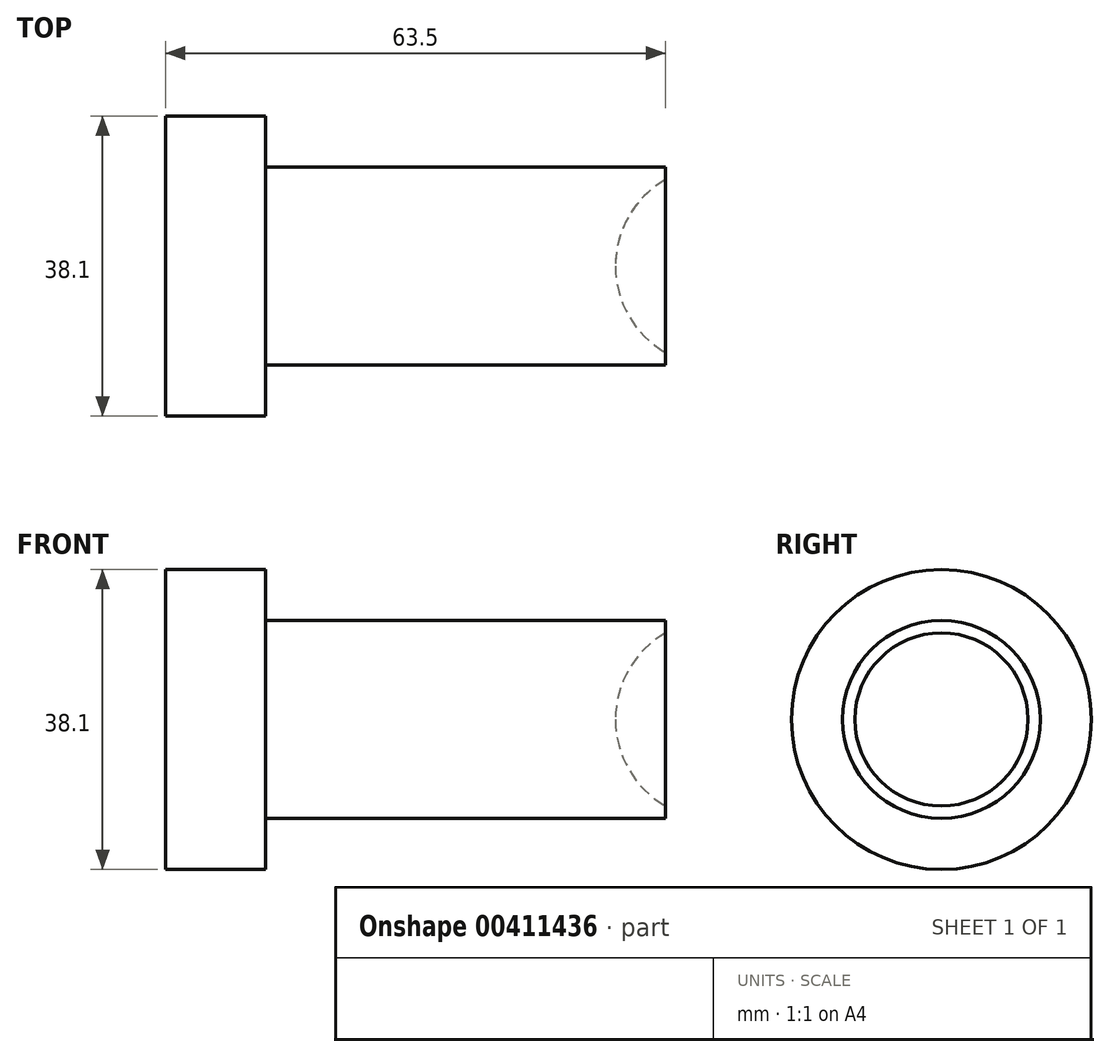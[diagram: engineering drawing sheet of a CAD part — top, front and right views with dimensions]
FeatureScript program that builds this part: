
annotation { "Feature Type Name" : "Feature", "Feature Type Description" : "" }
export const myFeature = defineFeature(function(context is Context, id is Id, definition is map)
    precondition{}
    {
        {
            var Q0;
            Q0=qCreatedBy(makeId("Right.planeOp"),FACE);
            var sketch = newSketch(context, id + "F0", { "sketchPlane" : qUnion([Q0])});
            skCircle(sketch, "E0", {"center": v(0, 0) * mm, "radius": 19.05 * mm});
            skSolve(sketch);
        }
        {
            var Q0;
            Q0 = qSketchRegion(id + "F0", true);
            extrude(context, id + "F1", {"entities" : qUnion([Q0]), "depth" : 12.7 * mm});
        }
        {
            var Q0;
            Q0=makeQuery(id+"F1.opExtrude","CAP_FACE",FACE,{"disambiguationData":[OSD([sQuery(id+"F0.wireOp",EDGE,"E0")])],"isStart":false});
            var sketch = newSketch(context, id + "F2", { "sketchPlane" : qUnion([Q0])});
            skCircle(sketch, "E1", {"center": v(0, 0) * mm, "radius": 12.57 * mm});
            skSolve(sketch);
        }
        {
            var Q0;
            Q0 = qSketchRegion(id + "F2", true);
            extrude(context, id + "F3", {"entities" : qUnion([Q0]), "operationType" : NewBodyOperationType.ADD, "depth" : 50.8 * mm});
        }
        {
            var Q0;
            Q0=qCreatedBy(makeId("Top.planeOp"),FACE);
            var sketch = newSketch(context, id + "F4", { "sketchPlane" : qUnion([Q0])});
            skArc(sketch, "E2", {"start": v(63.5, 11) * mm, "mid": v(58.85, 6.35) * mm, "end": v(57.15, 0) * mm});
            skLineSegment(sketch, "E3", {"start": v(63.5, 0) * mm, "end": v(57.15, 0) * mm});
            skLineSegment(sketch, "E4", {"start": v(63.5, 0) * mm, "end": v(63.5, 11) * mm});
            skSolve(sketch);
        }
        {
            var Q0;
            Q0=qCreatedBy(makeId("Top.planeOp"),FACE);
            var sketch = newSketch(context, id + "F5", { "sketchPlane" : qUnion([Q0])});
            skLineSegment(sketch, "E5", {"start": v(92.71, 0) * mm, "end": v(43.19, 0) * mm, "construction": true});
            skSolve(sketch);
        }
        {
            var Q0;
            Q0 = qSketchRegion(id + "F4", true);
            var Q1;
            Q1=sQuery(id+"F5.wireOp",EDGE,"E5");
            revolve(context, id + "F6", {"operationType" : NewBodyOperationType.REMOVE, "entities" : qUnion([Q0]), "axis" : qUnion([Q1]), "revolveType" : RevolveType.FULL, "oppositeDirection" : true});
        }
    });
